# Revit family: Homefield Pendant 450
name_source: partatom
category: Lighting Fixtures
revit_build: Autodesk Revit 2018 (Build: 20170927_1515(x64)
units: mm (PartAtom-declared; Revit-internal decimal feet)

## family parameters
Always vertical = Yes
Cut with Voids When Loaded = No
Host = Ceiling
Light Source = No
OmniClass Number = 23.80.70.11
OmniClass Title = Luminaries for Internal Lighting
Part Type = Normal
Room Calculation Point = No
Round Connector Dimension = Use Diameter
Shared = No

## types (2) — shared parameters

## per-type parameters (varying)
| type | ADA compliant | Dimmable | Dimming Method | Driver Included | Driver Required | Efficacy (lm/w) | Electrical Class | Lamp | Length of supplied cable | Light Source Fixed | Location Rating | Main Finish | Main Material | Max Drop (pendants) | Power (Watts) | Product Code | Product Location | Product Name | Product SKU |
| CE | Not Applicable | Lamp Dependent | Lamp Dependent | Not Applicable | No | Lamp Dependent | Class II | E27 60W Max | 1500mm | Yes | IP23 | Textured Black | Mild Steel | 1500mm | 60W Max | 1095033 | Outdoor | Homefield Pendant 450 | 1095033 |
| ETL |  |  |  |  |  |  |  |  |  |  |  |  |  |  |  |  |  |  |  |

## geometry (parser evidence)
native form markers: Sweep x2
no freeform markers — native parametric forms only
